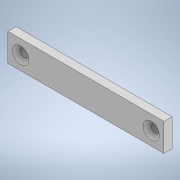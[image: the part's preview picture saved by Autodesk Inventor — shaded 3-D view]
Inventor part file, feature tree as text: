
AUTODESK INVENTOR PART (.ipt)
format: ipt  version: 2021 (Build 250183000, 183)  size: 111,104 bytes
history: native  units: mm
features: sketch x2, extrude x1, hole x1
ambient origin geometry x8: Origin, YZ Plane, XZ Plane, XY Plane, X Axis, Y Axis, Z Axis, Center Point
bodies: Solid1 (feature_tree)
feature tree (4):
  extrude  "Extrusion1"  Depth=6.8mm
  hole  "Hole1"  [1 undecoded]
  sketch  "Sketch1"  dims[d0=38.2mm d1=6.8mm]
  sketch  "Sketch2"  dims[d2=19.1mm d3=3.4mm d4=2.0mm d5=0.0mm d6=3.5mm d7=3.5mm d8=32.0mm d9=3.1mm d10=3.1mm d11=2.0mm d12=6.0mm d13=4.0mm d14=2.0mm d15=90.0deg d16=4.0mm d17=20.594885mm]
note: 1 required parameter value undecoded (feature->parameter linkage not recoverable at this tier; creation-order binding heuristic only, values carry confidence <= 0.55)
